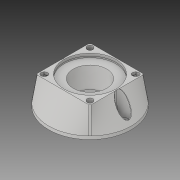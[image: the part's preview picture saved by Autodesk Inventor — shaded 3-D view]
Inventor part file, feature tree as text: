
AUTODESK INVENTOR PART (.ipt)
format: ipt  version: 2019 (Build 230136000, 136)  size: 670,720 bytes
history: native  units: in
note: dims shown in document units (in); Inventor stores cm internally (conversion verified against a paired STEP export)
features: fillet x1
ambient origin geometry x8: Origin, YZ Plane, XZ Plane, XY Plane, X Axis, Y Axis, Z Axis, Center Point
bodies: Solid1 (feature_tree)
feature tree (1):
  fillet  "Fillet3"  [1 undecoded]
note: 1 required parameter value undecoded (feature->parameter linkage not recoverable at this tier; creation-order binding heuristic only, values carry confidence <= 0.55)
